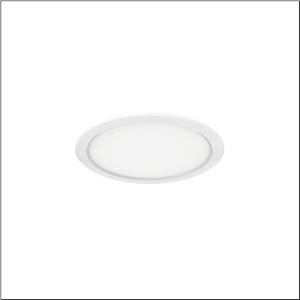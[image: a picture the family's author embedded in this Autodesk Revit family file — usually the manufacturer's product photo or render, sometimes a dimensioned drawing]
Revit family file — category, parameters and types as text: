
# Revit family: lunis_41_eco_51ds107f44b
name_source: partatom
category: Lighting Fixtures
units: mm (PartAtom-declared; Revit-internal decimal feet)

## family parameters
Cut with Voids When Loaded = No
Host = Face
Light Source = No
Part Type = Normal
Room Calculation Point = No
Round Connector Dimension = Use Diameter
Shared = No

## types (1)
- Lunis 41 Eco (1 x LED, 2300 lm, 17.5 W, 4000K)
    Apparent Load = 18 VA
    CIE Flux Codes = 47 80 97 100 100
    Color Rendering = 80
    Color Temperature = 4000K
    Default Elevation = 1800 mm
    Description = Lunis 41 Eco, downlight, light emission: direct distribution, LED rated luminous flux: 2.300lm, light colour: 840, mains connection: 230V, AC, 50/60Hz, housing, round, of aluminium, coated, traffic white (RAL 9016), diameter: 216mm, recess depth: 58mm, protection rating (complete): IP20, protection rating (on room side): IP40, insulation class (complete): insulation class II (safety insulation), certification: CE, permissible ambient temperature for indoor applications: -20..+40°C, packaging unit: 1 piece
    Height = 0 mm  [stored 0 ft]
    Lamp = 1 x LED
    Lamp Light Flux = 2300 lm
    Lamp Power = 17.5 W
    Lamp count = 1
    Length = 216 mm
    Luminous efficacy = 131 lm/W
    Manufacturer = Siteco
    ModVariant = No
    Model = 51DS107F44B
    Mounting Place = Ceiling
    Mounting Type = Recessed
    Number of Poles = 1
    OnlyDefault = Yes
    Power Factor = 1
    Product Name = Lunis 41 Eco
    Product group = downlight
    ProductGroupID = 401
    Protection Class = Protection class II
    Protection Degree = IP 20
    RLX_Detail_Level = 1
    RLX_Emergency_Light_Flux = 0 lm
    RLX_Emergency_Type = 0
    RLX_Emergency_Type_DB = No
    RlxData = <blob elided: 10221 chars, md5=4129a24d>
    Socket = socket
    Standby Power = 0 W
    System Light Flux = 2300 lm
    System Power = 18 W
    Type Comments = Product without accessories
    Type Image = l_1345914.jpg
    URL = http://relux.com
    VarID = ---
    Voltage = 0 V
    Weight = 0.00 kg
    Width = 0 mm  [stored 0 ft]

note: [stored X ft] marks values corroborated as IEEE doubles in the binary element streams (Revit-internal decimal feet)

## geometry (parser evidence)
native form markers: Sweep x9
no freeform markers — native parametric forms only
